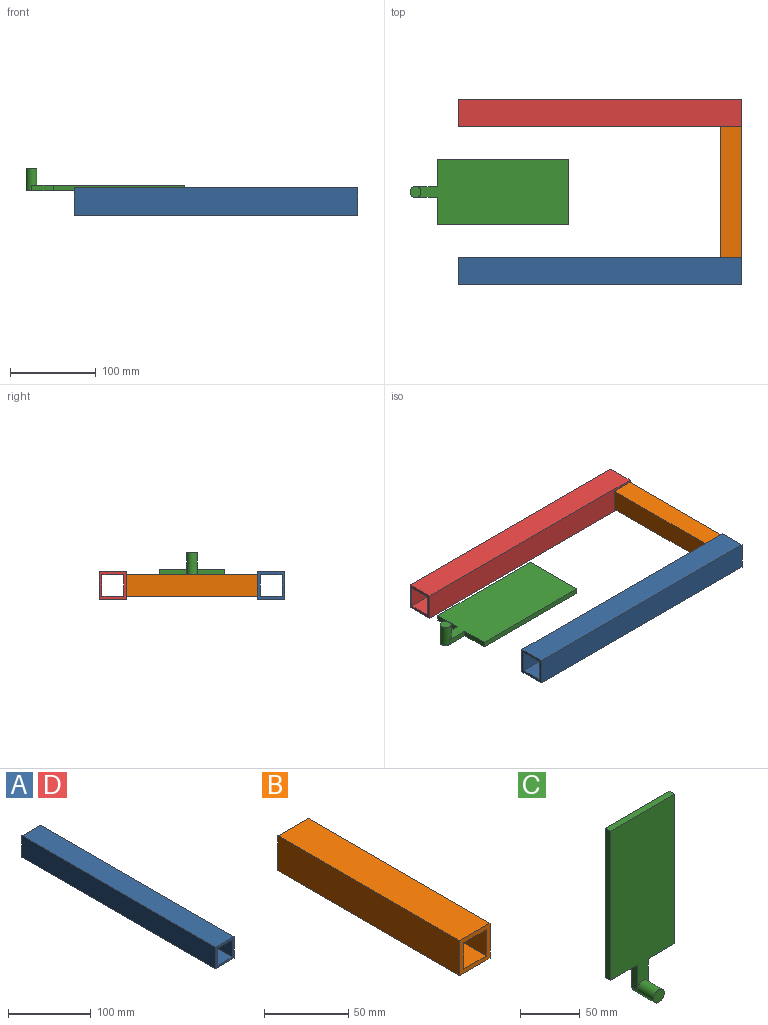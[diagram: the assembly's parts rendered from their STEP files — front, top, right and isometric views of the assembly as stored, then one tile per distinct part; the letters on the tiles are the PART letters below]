
ASSEMBLY  parts=4 mates=3
PART A: 10 faces, bbox 31.8x330.2x31.8 mm
  f0: plane 330.2x25.4mm, normal (0,0,-1), area 8387.1mm2, adj f1,f7,f8,f9
  f1: plane 330.2x25.4mm, normal (-1,0,0), area 8387.1mm2, adj f0,f2,f8,f9
  f2: plane 330.2x25.4mm, normal (0,0,1), area 8387.1mm2, adj f1,f7,f8,f9
  f3: plane 330.2x31.75mm, normal (-1,0,0), area 10483.8mm2, adj f4,f6,f8,f9
  f4: plane 330.2x31.75mm, normal (0,0,-1), area 10483.8mm2, adj f3,f5,f8,f9
  f5: plane 330.2x31.75mm, normal (1,0,0), area 10483.8mm2, adj f4,f6,f8,f9
  f6: plane 330.2x31.75mm, normal (0,0,1), area 10483.8mm2, adj f3,f5,f8,f9
  f7: plane 330.2x25.4mm, normal (1,0,0), area 8387.1mm2, adj f0,f2,f8,f9
  f8: plane 31.75x31.75mm, normal (0,-1,0), area 362.9mm2, adj f0,f1,f2,f3,f4,f5,f6,f7
  f9: plane 31.75x31.75mm, normal (0,1,0), area 362.9mm2, adj f0,f1,f2,f3,f4,f5,f6,f7
PART B: 11 faces, bbox 25.4x152.4x25.4 mm
  f0: plane 152.4x25.4mm, normal (1,0,0), area 3871mm2, adj f1,f3,f4,f5
  f1: plane 152.4x25.4mm, normal (0,0,1), area 3871mm2, adj f0,f2,f4,f5
  f2: plane 152.4x25.4mm, normal (-1,0,0), area 3871mm2, adj f1,f3,f4,f5
  f3: plane 152.4x25.4mm, normal (0,0,-1), area 3871mm2, adj f0,f2,f4,f5
  f4: plane 25.4x25.4mm, normal (0,-1,0), area 282.3mm2, adj f0,f1,f2,f3,f6,f7,f8,f9
  f5: plane 25.4x25.4mm, normal (0,1,0), area 645.2mm2, adj f0,f1,f2,f3
  f6: plane 149.23x19.05mm, normal (-1,0,0), area 2842.7mm2, adj f4,f7,f9,f10
  f7: plane 149.23x19.05mm, normal (0,0,-1), area 2842.7mm2, adj f4,f6,f8,f10
  f8: plane 149.23x19.05mm, normal (1,0,0), area 2842.7mm2, adj f4,f7,f9,f10
  f9: plane 149.23x19.05mm, normal (0,0,1), area 2842.7mm2, adj f4,f6,f8,f10
  f10: plane 19.05x19.05mm, normal (0,-1,0), area 362.9mm2, adj f6,f7,f8,f9
PART C: 11 faces, bbox 76.2x25.4x184.2 mm
  f0: cylinder r=6.35mm len=25.4mm, axis (0,1,0), area 886.7mm2, adj f1,f2,f7,f8,f10
  f1: plane 12.7x12.7mm, normal (0,-1,0), area 126.7mm2, adj f0
  f2: plane 184.15x76.2mm, normal (0,1,0), area 11998.8mm2, adj f0,f3,f4,f5,f6,f7,f8,f9
  f3: plane 152.4x6.35mm, normal (1,0,0), area 967.7mm2, adj f2,f4,f9,f10
  f4: plane 76.2x6.35mm, normal (0,0,1), area 483.9mm2, adj f2,f3,f5,f10
  f5: plane 152.4x6.35mm, normal (-1,0,0), area 967.7mm2, adj f2,f4,f6,f10
  f6: plane 31.75x6.35mm, normal (0,0,-1), area 201.6mm2, adj f2,f5,f7,f10
  f7: plane 25.4x6.35mm, normal (-1,0,0), area 161.3mm2, adj f0,f2,f6,f10
  f8: plane 25.4x6.35mm, normal (1,0,0), area 161.3mm2, adj f0,f2,f9,f10
  f9: plane 31.75x6.35mm, normal (0,0,-1), area 201.6mm2, adj f2,f3,f8,f10
  f10: plane 177.8x76.2mm, normal (0,-1,0), area 11872.1mm2, adj f0,f3,f4,f5,f6,f7,f8,f9
PART D: same geometry as A
PLACE A rot(axis=(0,0,-1),90deg) t=(-4.34,-95.93,-156.9)mm
PLACE B t=(-17.04,72.34,-156.9)mm fixed
PLACE C rot(axis=(-0.58,0.58,-0.58),120deg) t=(-282.4,-3.86,-144.2)mm
PLACE D rot(axis=(0.71,0.71,0),180deg) t=(-4.34,88.22,-156.9)mm
MATE fastened B.f5 <-> D.f3  axis (0,1,0) through (-4.34,72.34,-156.9)mm
MATE fastened A.f3 <-> B.f4  axis (0,1,0) through (-4.34,-80.06,-156.9)mm
MATE planar B.f1 <-> C.f2  axis (0,0,1) through (-17.04,-3.86,-144.2)mm
